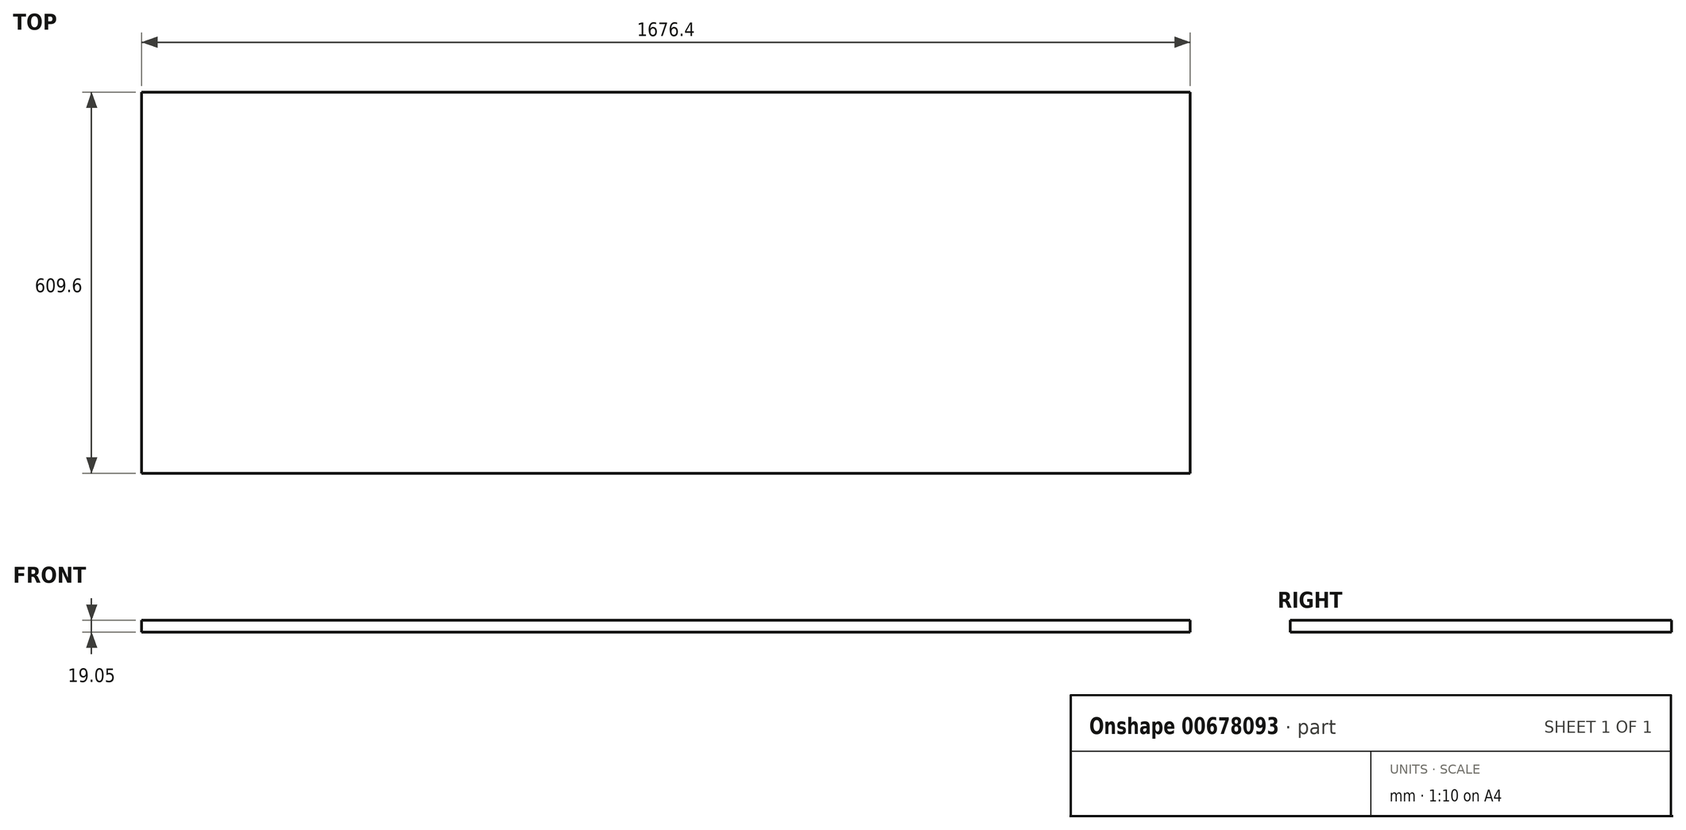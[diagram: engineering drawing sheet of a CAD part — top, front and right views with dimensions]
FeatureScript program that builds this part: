
annotation { "Feature Type Name" : "Feature", "Feature Type Description" : "" }
export const myFeature = defineFeature(function(context is Context, id is Id, definition is map)
    precondition{}
    {
        {
            var Q0;
            Q0=qCreatedBy(makeId("Top.planeOp"),FACE);
            var sketch = newSketch(context, id + "F0", { "sketchPlane" : qUnion([Q0])});
            skLineSegment(sketch, "E0.bottom", {"start": v(838.2, 304.8) * mm, "end": v(-838.2, 304.8) * mm});
            skLineSegment(sketch, "E0.top", {"start": v(838.2, -304.8) * mm, "end": v(-838.2, -304.8) * mm});
            skLineSegment(sketch, "E0.left", {"start": v(838.2, 304.8) * mm, "end": v(838.2, -304.8) * mm});
            skLineSegment(sketch, "E0.right", {"start": v(-838.2, 304.8) * mm, "end": v(-838.2, -304.8) * mm});
            skPoint(sketch, "E0.middle", {"position": v(0, 0) * mm});
            skSolve(sketch);
        }
        {
            var Q0;
            Q0=makeQuery(id+"F0.imprint","IMPRINT",FACE,{"disambiguationData":[TD([[makeQuery(id+"F0.imprint","IMPRINT",EDGE,{"derivedFrom":sQuery(id+"F0.wireOp",EDGE,"E0.bottom")}),1.0]])]});
            extrude(context, id + "F1", {"entities" : qUnion([Q0]), "depth" : 19.05 * mm, "offsetDistance" : 25.4 * mm});
        }
    });
